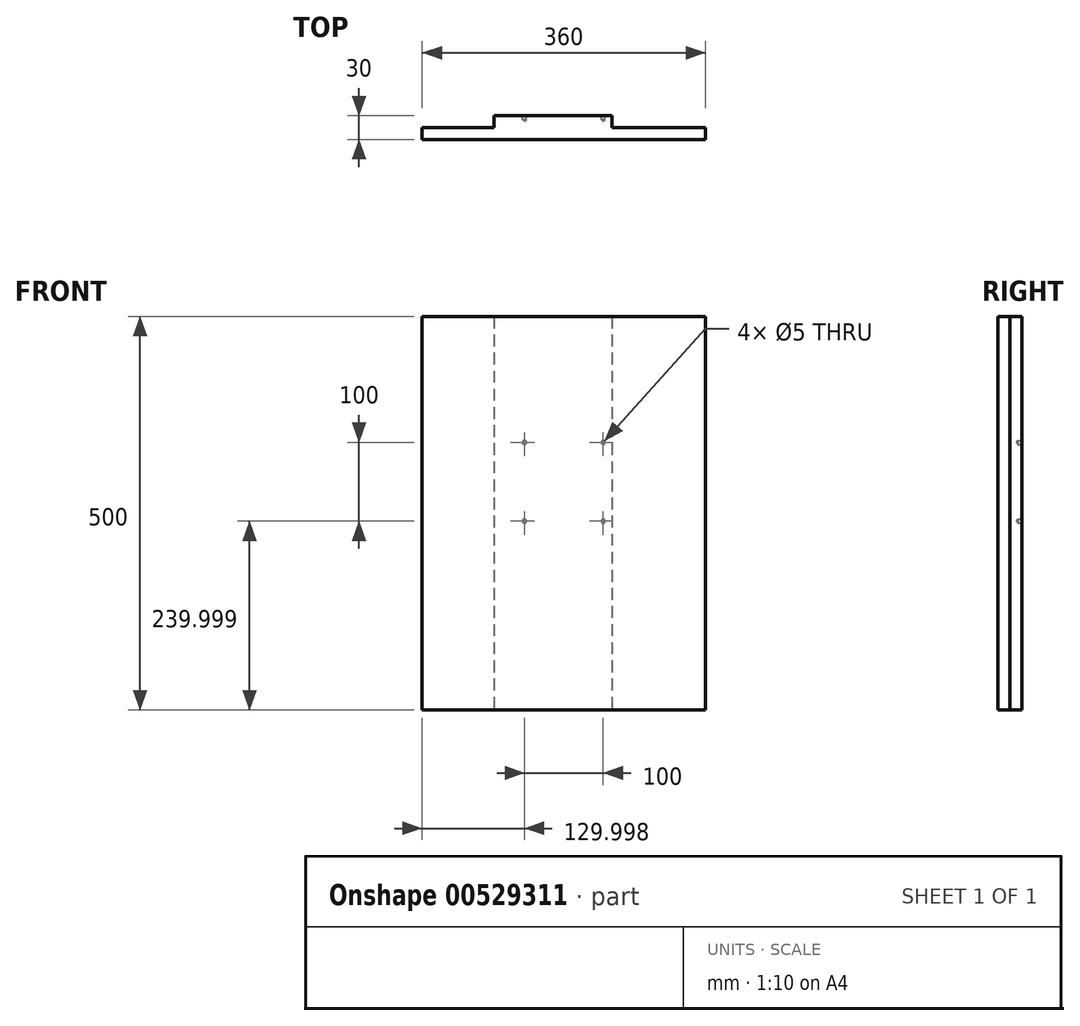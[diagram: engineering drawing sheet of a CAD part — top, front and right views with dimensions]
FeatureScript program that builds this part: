
annotation { "Feature Type Name" : "Feature", "Feature Type Description" : "" }
export const myFeature = defineFeature(function(context is Context, id is Id, definition is map)
    precondition{}
    {
        {
            var Q0;
            Q0=qCreatedBy(makeId("Front.planeOp"),FACE);
            var sketch = newSketch(context, id + "F0", { "sketchPlane" : qUnion([Q0])});
            skLineSegment(sketch, "E0.bottom", {"start": v(-201, -247.88) * mm, "end": v(159, -247.88) * mm});
            skLineSegment(sketch, "E0.top", {"start": v(-201, 252.12) * mm, "end": v(159, 252.12) * mm});
            skLineSegment(sketch, "E0.left", {"start": v(-201, -247.88) * mm, "end": v(-201, 252.12) * mm});
            skLineSegment(sketch, "E0.right", {"start": v(159, -247.88) * mm, "end": v(159, 252.12) * mm});
            skSolve(sketch);
        }
        {
            var Q0;
            Q0=makeQuery(id+"F0.imprint","IMPRINT",FACE,{"disambiguationData":[TD([[makeQuery(id+"F0.imprint","IMPRINT",EDGE,{"derivedFrom":sQuery(id+"F0.wireOp",EDGE,"E0.bottom")}),1.0]])]});
            extrude(context, id + "F1", {"entities" : qUnion([Q0]), "oppositeDirection" : true, "depth" : 15 * mm, "offsetDistance" : 25 * mm});
        }
        {
            var Q0;
            Q0=makeQuery(id+"F1.opExtrude","CAP_FACE",FACE,{"disambiguationData":[OSD([sQuery(id+"F0.wireOp",EDGE,"E0.bottom"),sQuery(id+"F0.wireOp",EDGE,"E0.top"),sQuery(id+"F0.wireOp",EDGE,"E0.left"),sQuery(id+"F0.wireOp",EDGE,"E0.right")])],"isStart":false});
            var sketch = newSketch(context, id + "F2", { "sketchPlane" : qUnion([Q0])});
            skLineSegment(sketch, "E1.bottom", {"start": v(-40.25, 252.12) * mm, "end": v(109.75, 252.12) * mm});
            skLineSegment(sketch, "E1.top", {"start": v(-40.25, -247.88) * mm, "end": v(109.75, -247.88) * mm});
            skLineSegment(sketch, "E1.left", {"start": v(-40.25, 252.12) * mm, "end": v(-40.25, -247.88) * mm});
            skLineSegment(sketch, "E1.right", {"start": v(109.75, 252.12) * mm, "end": v(109.75, -247.88) * mm});
            skSolve(sketch);
        }
        {
            var Q0;
            Q0=makeQuery(id+"F2.imprint","IMPRINT",FACE,{"disambiguationData":[TD([[makeQuery(id+"F2.imprint","IMPRINT",EDGE,{"derivedFrom":sQuery(id+"F2.wireOp",EDGE,"E1.bottom")}),1.0]])]});
            extrude(context, id + "F3", {"entities" : qUnion([Q0]), "operationType" : NewBodyOperationType.ADD, "depth" : 15 * mm, "offsetDistance" : 25 * mm});
        }
        {
            var Q0;
            Q0=makeQuery(id+"F3.opExtrude","CAP_FACE",FACE,{"disambiguationData":[OSD([sQuery(id+"F2.wireOp",EDGE,"E1.bottom"),sQuery(id+"F2.wireOp",EDGE,"E1.top"),sQuery(id+"F2.wireOp",EDGE,"E1.left"),sQuery(id+"F2.wireOp",EDGE,"E1.right")])],"isStart":false});
            var sketch = newSketch(context, id + "F4", { "sketchPlane" : qUnion([Q0])});
            skLineSegment(sketch, "E2.bottom", {"start": v(-29, 92.12) * mm, "end": v(71, 92.12) * mm, "construction": true});
            skLineSegment(sketch, "E2.top", {"start": v(-29, -7.88) * mm, "end": v(71, -7.88) * mm, "construction": true});
            skLineSegment(sketch, "E2.left", {"start": v(-29, 92.12) * mm, "end": v(-29, -7.88) * mm, "construction": true});
            skLineSegment(sketch, "E2.right", {"start": v(71, 92.12) * mm, "end": v(71, -7.88) * mm, "construction": true});
            skPoint(sketch, "E3", {"position": v(-29, 92.12) * mm});
            skPoint(sketch, "E4", {"position": v(71, 92.12) * mm});
            skPoint(sketch, "E5", {"position": v(71, -7.88) * mm});
            skPoint(sketch, "E6", {"position": v(-29, -7.88) * mm});
            skSolve(sketch);
        }
        {
            var Q0;
            Q0=sQuery(id+"F4.wireOp",VERTEX,"E3");
            var Q1;
            Q1=sQuery(id+"F4.wireOp",VERTEX,"E4");
            var Q2;
            Q2=sQuery(id+"F4.wireOp",VERTEX,"E5");
            var Q3;
            Q3=sQuery(id+"F4.wireOp",VERTEX,"E6");
            var Q4;
            Q4=makeQuery(id+"F1.opExtrude","SWEPT_BODY",BODY,{"disambiguationData":[OSD([sQuery(id+"F0.wireOp",EDGE,"E0.bottom"),sQuery(id+"F0.wireOp",EDGE,"E0.top"),sQuery(id+"F0.wireOp",EDGE,"E0.left"),sQuery(id+"F0.wireOp",EDGE,"E0.right")])]});
            hole(context, id + "F5", {"style" : HoleStyle.SIMPLE, "endStyle" : HoleEndStyle.BLIND, "holeDiameter" : 5 * mm, "holeDepth" : 5 * mm, "isTappedThrough" : true, "tappedDepth" : 12 * mm, "tapClearance" : 3, "locations" : qUnion([Q0, Q1, Q2, Q3]), "scope" : qUnion([Q4])});
        }
    });
